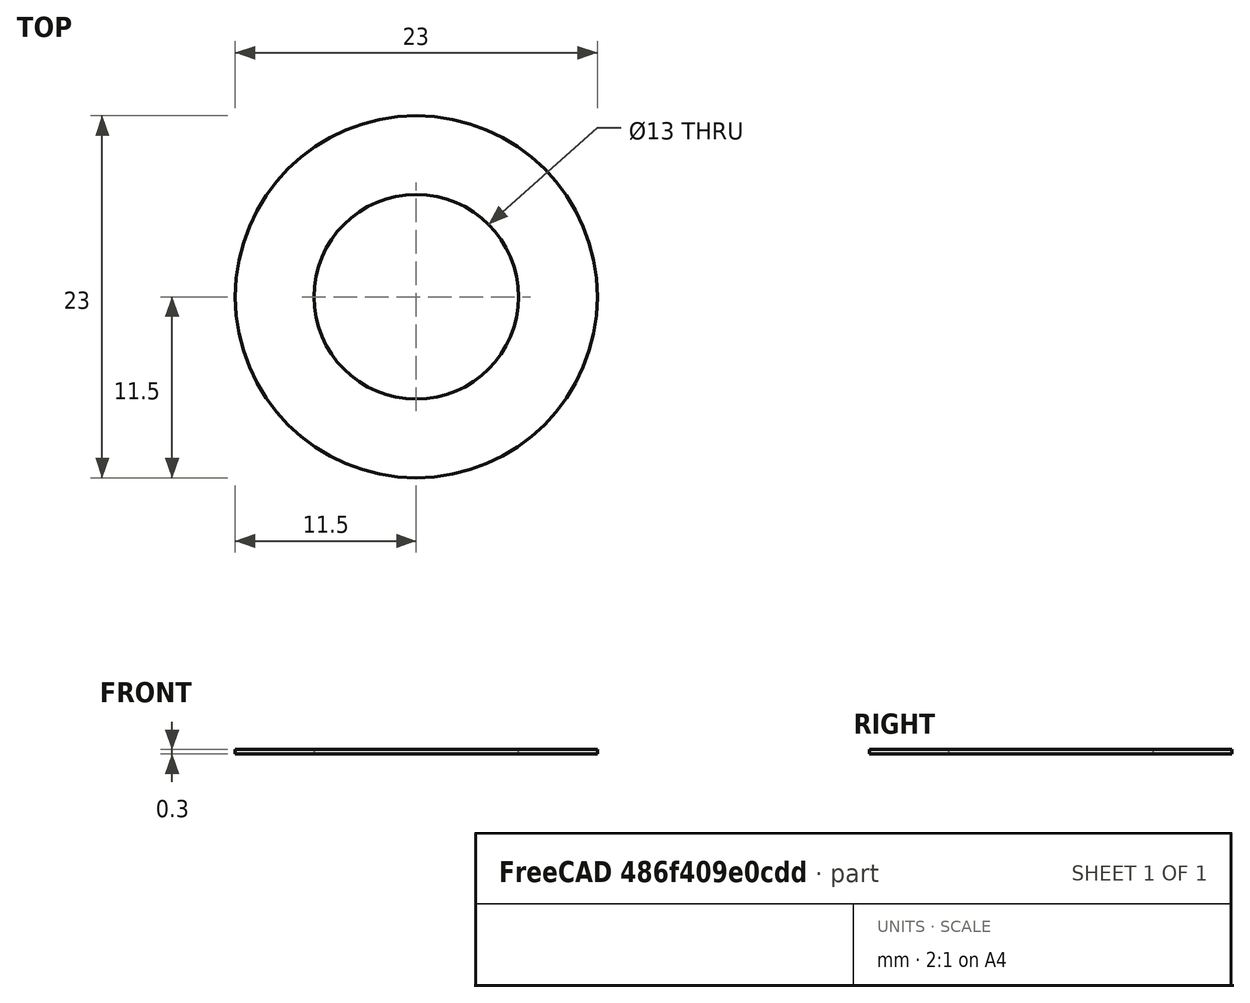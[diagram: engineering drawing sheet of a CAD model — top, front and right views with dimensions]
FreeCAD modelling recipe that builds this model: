
FCSTD DOCUMENT  (FreeCAD 0.19R24276 (Git))
Label: Ring_d13_d23_h0_3_v4
License: All rights reserved
LicenseURL: http://en.wikipedia.org/wiki/All_rights_reserved
objects: Sketcher::SketchObject×1, PartDesign::Pad×1, PartDesign::Body×1
note: 4 computed .brp shape members not serialized (recipe doc carries the construction recipe); baked Part::Feature solids carry a one-line shape summary decoded from their .brp

FEATURE [Sketcher::SketchObject] Sketch
  FullyConstrained = true
  MapMode = 5
  Support = -> [XY_Plane]
  sketch-geometry (2):
    g0: Circle CenterX=0 CenterY=0 CenterZ=0 NormalX=0 NormalY=0 NormalZ=1 AngleXU=0 Radius=6.5
    g1: Circle CenterX=0 CenterY=0 CenterZ=0 NormalX=0 NormalY=0 NormalZ=1 AngleXU=0 Radius=11.5
  constraints (4):
    c: Coincident(g0,g-1)
    c: Coincident(g1,g0)
    c: Diameter(g0) = 13
    c: Diameter(g1) = 23
FEATURE [PartDesign::Pad] Pad
  Direction = (1,1,1)
  Length = 0.3
  Length2 = 100
  Profile = -> Sketch
  Type = 0
FEATURE [PartDesign::Body] Body
  Group = -> [Sketch,Pad]
  Origin = -> Origin
  Tip = -> Pad
